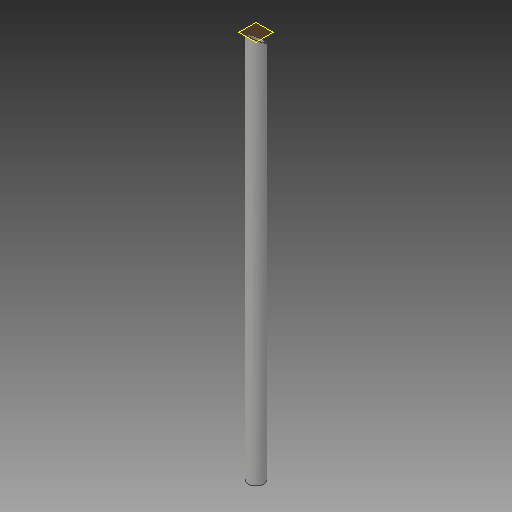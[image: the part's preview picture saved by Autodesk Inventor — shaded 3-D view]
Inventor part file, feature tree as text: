
AUTODESK INVENTOR PART (.ipt)
format: ipt  version: 2018 (Build 220112000, 112)  size: 86,528 bytes
history: native  units: mm
features: extrude x2, sketch x2, plane x1
ambient origin geometry x8: Origin, YZ Plane, XZ Plane, XY Plane, X Axis, Y Axis, Z Axis, Center Point
bodies: Solid1 (feature_tree)
feature tree (5):
  extrude  "Extrusion1"  Depth=3.75mm
  extrude  "skrå ende"  Depth=10.0mm TaperAngle=0.0deg
  plane  "Work Plane3"
  sketch  "Sketch1"  dims[d0=48.5mm d1=3.75mm]
  sketch  "Sketch2"  dims[d2=41.0mm d3=1200.0mm d4=0.0mm d5=5.986479mm d6=10.0mm d7=0.0mm]
